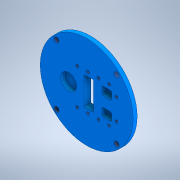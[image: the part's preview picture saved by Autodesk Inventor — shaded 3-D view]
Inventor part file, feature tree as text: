
AUTODESK INVENTOR PART (.ipt)
format: ipt  version: 2021 (Build 250183000, 183)  size: 219,136 bytes
history: native  units: mm
features: extrude x4, sketch x3, hole x2, other x1
ambient origin geometry x8: Origin, YZ Plane, XZ Plane, XY Plane, X Axis, Y Axis, Z Axis, Center Point
bodies: Body1 (feature_tree)
feature tree (10):
  other  "Sólido1"
  extrude  "Extrusión1"  Depth=3.2mm TaperAngle=0.0deg
  sketch  "Boceto2"  dims[d3=50.0mm d4=32.0mm d5=12.0mm d6=11.65mm d7=10.5mm d8=7.0mm d9=21.0mm d10=2.8mm d11=4.4mm d12=5.6mm d13=4.4mm d14=0.8mm d15=0.8mm d16=0.8mm d17=0.8mm d18=0.8mm d19=0.8mm d20=2.0mm d21=2.0mm d22=2.0mm d23=2.0mm d24=2.0mm d25=2.0mm d26=2.0mm d27=2.0mm d28=2.0mm d29=2.0mm d30=3.2mm d31=0.0mm]
  extrude  "Extrusión2"  Depth=2.0mm
  extrude  "Extrusión3"  Depth=2.0mm
  sketch  "Boceto3"  dims[d32=5.0mm d33=0.0mm d34=70.0mm d35=58.0mm d36=3.0mm d37=0.0mm d40=32.0mm d41=45.0deg d42=3.0mm d43=40.0mm d45=360.0deg d47=3.688101mm d48=9.0mm d49=4.0mm d50=2.0mm d51=90.0deg d52=13.0mm d53=0.0mm d54=2.013mm d55=5.0mm d56=4.0mm d57=2.0mm d58=90.0deg d59=7.6mm d60=0.0mm d61=0.75mm d62=20.594885mm d63=0.0625mm d64=0.75mm d65=0.375mm]
  extrude  "Extrusión4"  Depth=3.0mm TaperAngle=0.0deg
  hole  "Agujero1"  [1 undecoded]
  hole  "Agujero2"  [1 undecoded]
  sketch  "Boceto1"  dims[d1=5.0mm d2=0.0mm]
note: 2 required parameter values undecoded (feature->parameter linkage not recoverable at this tier; creation-order binding heuristic only, values carry confidence <= 0.55)
